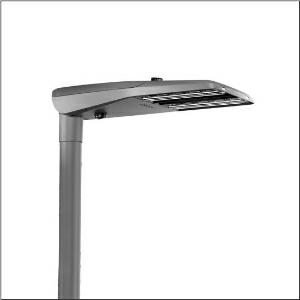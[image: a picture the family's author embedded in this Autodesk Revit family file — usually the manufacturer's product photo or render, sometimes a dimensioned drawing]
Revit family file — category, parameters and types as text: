
# Revit family: streetlight_sl_11_iq_midi___st1_2a_5xc3a11y08me_f942
name_source: partatom
category: Lighting Fixtures
units: mm (PartAtom-declared; Revit-internal decimal feet)

## family parameters
Cut with Voids When Loaded = No
Host = Face
Light Source = No
Part Type = Normal
Room Calculation Point = No
Round Connector Dimension = Use Diameter
Shared = No

## types (1)
- --- (1 x LED, 11200 lm, 123.4 W, 1800K)
    Apparent Load = 123 VA
    CIE Flux Codes = 32 70 96 100 100
    Color Rendering = 70
    Color Temperature = 1800K
    Default Elevation = 1800 mm
    Description = Streetlight SL 11 iQ midi, mast luminaire, primary light control with 3 zone facetted reflector, of plastic, silver coated, highly specular, primary optical cover: cover, of PMMA, transparent, light distribution: ST1.2a, light emission: direct distribution, primary light characteristic: asymmetric, installation type: post-top, side-entry, lamps: LED, High Power LED, rated values: 11.200lm | 123,4W | 90,8lm/W (begin service life); end service life: 11.200lm | 130,9W; at 50% lumin. flux: 5.600lm | 54,1W | 103,5lm/W, colour temperature: 1800K, colour rendering: CRI > 70, light colour: 718, light setting 1 begin service life: 100% | 11.200lm | 123,4W | 90,8lm/W | 1.800K, light setting 1 end service life: 130,9W, further light settings possible, control: pre-setting: logarithmic dimming characteristic, Street-Remote, Auto-Match, Temp-Guard, Lumen-Switch, Night-Set, Smart-Wire, Light-Fading, Desk-Remote (wireless, voltage-free reading and setting of iQ features in the workshop via application-optimized NFC function/RFID function), optimised constant luminous flux control (CLO 2.0), with cable H07RN-F 3x 1.5mm², mains connection: 230..240V, AC, 50/60Hz, connection cable pre-assembled, cable length: 12,5m, luminaire housing, of diecast aluminium, powder-coated, SITECO metallic grey (DB 702S), please order mast flange separately, inclination adjustable without tools: 0°, 5°, 10°, 15° (post-top) | 0°, -5°, -10°, -15° (side-entry), sealing non-destructively replaceable, multi-level sealing system, length: 780mm, width: 376mm, height: 118mm, mast flange for spigot size: 42mm (side-entry): 5XC10008XM4, 60/48mm (side-entry/post-top): 5XC10108XM2, 76/60mm (side-entry/post-top): 5XC10108XM1, equipment: Power, Smart Interface below and above, protection rating (complete): IP66, insulation class (complete): insulation class II (safety insulation), certification: CE, ENEC, ENEC+, VDE, UKCA, impact resistance: IK10, permissible operating ambient temperature for outdoor applications: -25..+50°C, standard-compliant lighting for roads and squares, Environmental Product Declaration (EPD) tested and certified by an independent institute, packaging unit: 1 piece

Light Distribution: ST1.2a
    Height = 118 mm
    Lamp = 1 x LED
    Lamp Light Flux = 11200 lm
    Lamp Power = 123.4 W
    Lamp count = 1
    Length = 780 mm
    Luminous efficacy = 91 lm/W
    Manufacturer = Siteco
    ModVariant = No
    Model = 5XC3A11Y08ME
    Number of Poles = 1
    OnlyDefault = Yes
    Power Factor = 1
    Product Name = Streetlight SL 11 iQ midi | ST1.2a
    Product group = mast luminaire | pylon top
    ProductGroupID = 6100
    Protection Class = Protection class II
    Protection Degree = IP 66
    RLX_Detail_Level = 1
    RLX_Emergency_Light_Flux = 0 lm
    RLX_Emergency_Type = 0
    RLX_Emergency_Type_DB = No
    RlxData = <blob elided: 70057 chars, md5=69d43e3d>
    Socket = socket
    Standby Power = 0 W
    System Light Flux = 11200 lm
    System Power = 123 W
    Type Comments = factory setting: luminous flux: 100 % | dim-lin: 254 | 553 mA
    Type Image = l_1004429.jpg
    URL = http://relux.com
    VarID = @adj_047287
    Voltage = 0 V
    Weight = 0.00 kg
    Width = 376 mm

## geometry (parser evidence)
native form markers: Blend x4, Sweep x11
no freeform markers — native parametric forms only
